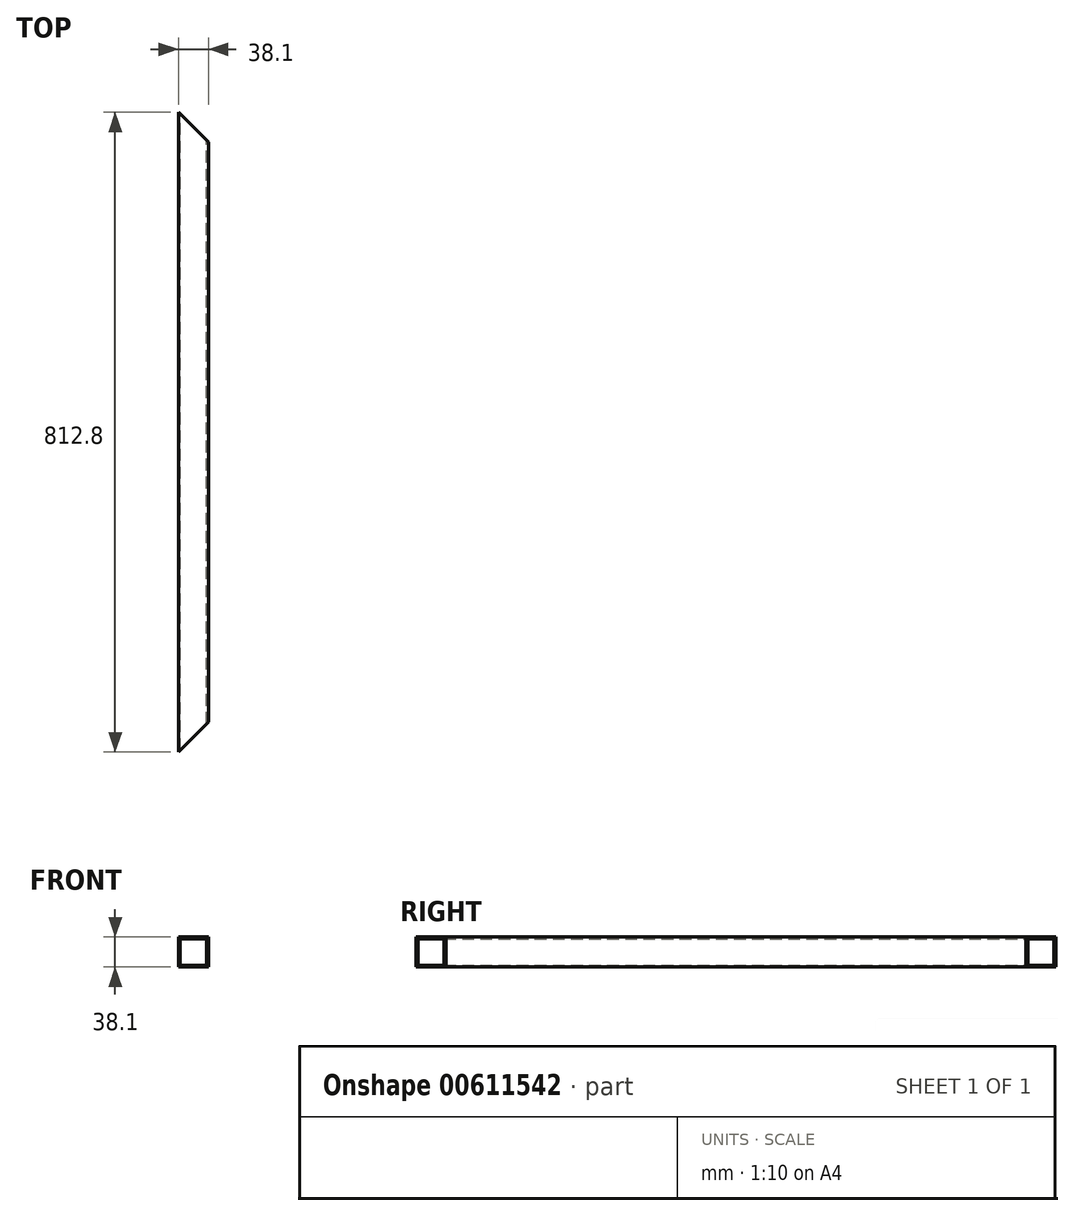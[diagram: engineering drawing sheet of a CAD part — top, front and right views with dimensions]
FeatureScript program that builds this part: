
annotation { "Feature Type Name" : "Feature", "Feature Type Description" : "" }
export const myFeature = defineFeature(function(context is Context, id is Id, definition is map)
    precondition{}
    {
        {
            var Q0;
            Q0=qCreatedBy(makeId("Front.planeOp"),FACE);
            var sketch = newSketch(context, id + "F0", { "sketchPlane" : qUnion([Q0])});
            skLineSegment(sketch, "E0.bottom", {"start": v(0, 0) * mm, "end": v(-38.1, 0) * mm});
            skLineSegment(sketch, "E0.top", {"start": v(0, -38.1) * mm, "end": v(-38.1, -38.1) * mm});
            skLineSegment(sketch, "E0.left", {"start": v(0, 0) * mm, "end": v(0, -38.1) * mm});
            skLineSegment(sketch, "E0.right", {"start": v(-38.1, 0) * mm, "end": v(-38.1, -38.1) * mm});
            skLineSegment(sketch, "E1.bottom", {"start": v(-35.81, -2.29) * mm, "end": v(-2.29, -2.29) * mm});
            skLineSegment(sketch, "E1.top", {"start": v(-35.81, -35.81) * mm, "end": v(-2.29, -35.81) * mm});
            skLineSegment(sketch, "E1.left", {"start": v(-35.81, -2.29) * mm, "end": v(-35.81, -35.81) * mm});
            skLineSegment(sketch, "E1.right", {"start": v(-2.29, -2.29) * mm, "end": v(-2.29, -35.81) * mm});
            skSolve(sketch);
        }
        {
            var Q0;
            Q0=qSketchRegion(id+"F0",true);
            extrude(context, id + "F1", {"entities" : qUnion([Q0]), "depth" : 812.8 * mm, "offsetDistance" : 25.4 * mm});
        }
        {
            var Q0;
            Q0=makeQuery(id+"F1.opExtrude","SWEPT_FACE",FACE,{"disambiguationData":[OSD([sQuery(id+"F0.wireOp",EDGE,"E0.bottom")])]});
            var sketch = newSketch(context, id + "F2", { "sketchPlane" : qUnion([Q0])});
            skLineSegment(sketch, "E2", {"start": v(-38.1, -812.8) * mm, "end": v(0, -774.7) * mm});
            skLineSegment(sketch, "E3", {"start": v(0, -774.7) * mm, "end": v(0, -812.8) * mm});
            skLineSegment(sketch, "E4", {"start": v(0, -812.8) * mm, "end": v(-38.1, -812.8) * mm});
            skLineSegment(sketch, "E5", {"start": v(-38.1, 0) * mm, "end": v(0, -38.1) * mm});
            skLineSegment(sketch, "E6", {"start": v(0, -38.1) * mm, "end": v(0, 0) * mm});
            skLineSegment(sketch, "E7", {"start": v(0, 0) * mm, "end": v(-38.1, 0) * mm});
            skSolve(sketch);
        }
        {
            var Q0;
            Q0=qSketchRegion(id+"F2",true);
            extrude(context, id + "F3", {"entities" : qUnion([Q0]), "operationType" : NewBodyOperationType.REMOVE, "oppositeDirection" : true, "depth" : 50.8 * mm, "offsetDistance" : 25.4 * mm});
        }
    });
